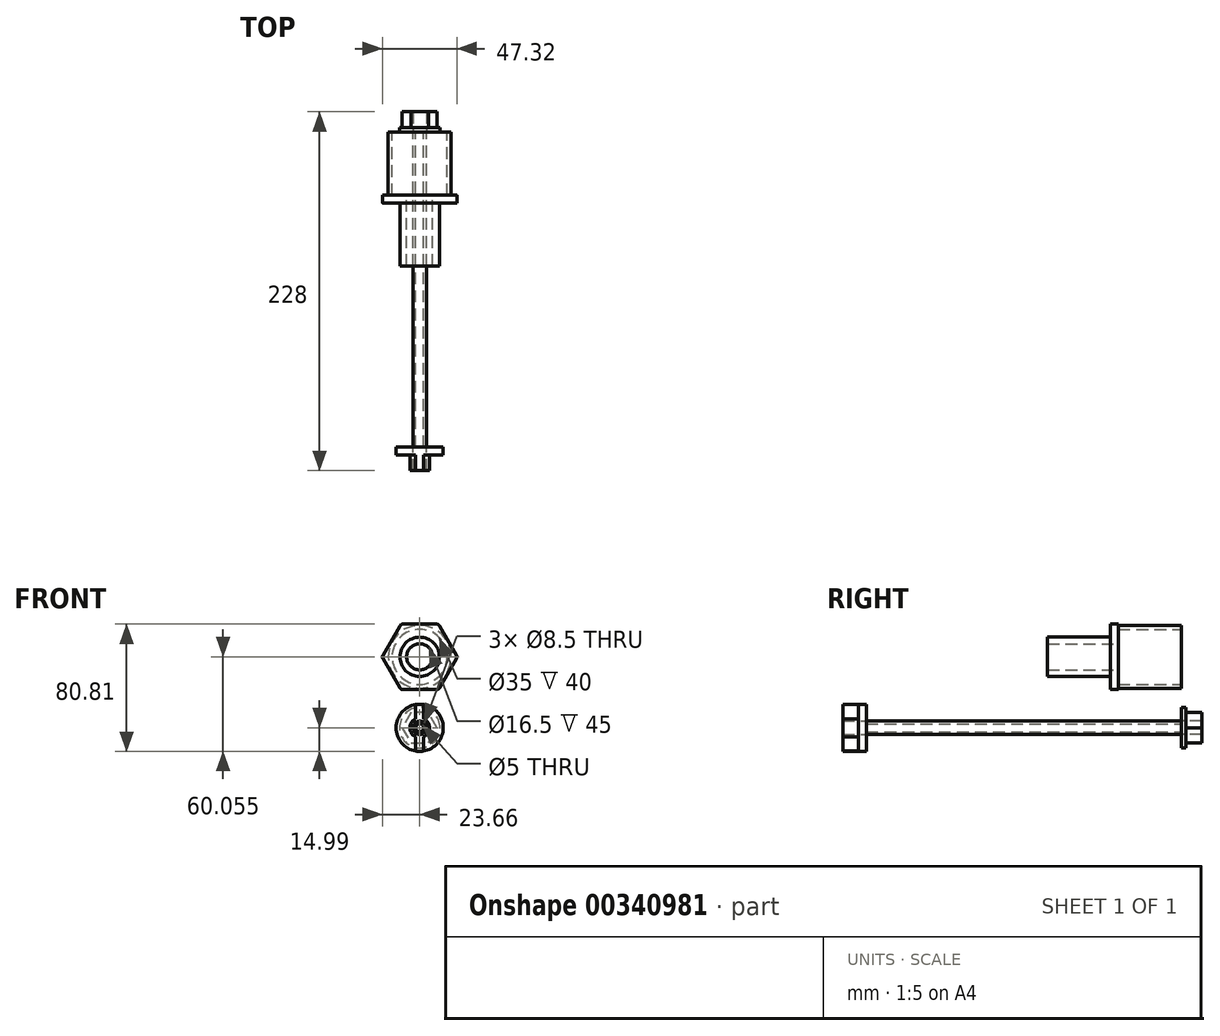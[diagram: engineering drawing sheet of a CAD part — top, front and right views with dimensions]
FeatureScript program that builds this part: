
annotation { "Feature Type Name" : "Feature", "Feature Type Description" : "" }
export const myFeature = defineFeature(function(context is Context, id is Id, definition is map)
    precondition{}
    {
        {
            var Q0;
            Q0=qCreatedBy(makeId("Front.planeOp"),FACE);
            var sketch = newSketch(context, id + "F0", { "sketchPlane" : qUnion([Q0])});
            skCircle(sketch, "E0", {"center": v(0, 0) * mm, "radius": 4.25 * mm});
            skCircle(sketch, "E1", {"center": v(0, 0) * mm, "radius": 2.5 * mm});
            skSolve(sketch);
        }
        {
            var Q0;
            Q0=makeQuery(id+"F0.imprint","IMPRINT",FACE,{"disambiguationData":[TD([[makeQuery(id+"F0.imprint","IMPRINT",EDGE,{"derivedFrom":sQuery(id+"F0.wireOp",EDGE,"E0")}),1.0]])]});
            extrude(context, id + "F1", {"entities" : qUnion([Q0]), "depth" : 200 * mm});
        }
        {
            var Q0;
            Q0=makeQuery(id+"F1.opExtrude","CAP_FACE",FACE,{"disambiguationData":[OSD([sQuery(id+"F0.wireOp",EDGE,"E0"),sQuery(id+"F0.wireOp",EDGE,"E1")])],"isStart":false});
            var sketch = newSketch(context, id + "F2", { "sketchPlane" : qUnion([Q0])});
            skCircle(sketch, "E2", {"center": v(0, 0) * mm, "radius": 4.25 * mm});
            skCircle(sketch, "E3", {"center": v(0, 0) * mm, "radius": 14.99 * mm});
            skSolve(sketch);
        }
        {
            var Q0;
            Q0=makeQuery(id+"F2.imprint","IMPRINT",FACE,{"disambiguationData":[TD([[makeQuery(id+"F2.imprint","IMPRINT",EDGE,{"derivedFrom":sQuery(id+"F2.wireOp",EDGE,"E2")}),-1.0]])]});
            extrude(context, id + "F3", {"entities" : qUnion([Q0]), "depth" : 5 * mm});
        }
        {
            var Q0;
            Q0=makeQuery(id+"F3.opExtrude","CAP_FACE",FACE,{"disambiguationData":[OSD([sQuery(id+"F2.wireOp",EDGE,"E2"),sQuery(id+"F2.wireOp",EDGE,"E3")])],"isStart":false});
            var sketch = newSketch(context, id + "F4", { "sketchPlane" : qUnion([Q0])});
            skCircle(sketch, "E4", {"center": v(0, 0) * mm, "radius": 14.99 * mm});
            skCircle(sketch, "E5", {"center": v(0, 0) * mm, "radius": 4.25 * mm});
            skCircle(sketch, "E6", {"center": v(0, 0) * mm, "radius": 6.25 * mm});
            skLineSegment(sketch, "E7", {"start": v(-2.5, 5.73) * mm, "end": v(-2.5, 14.78) * mm});
            skLineSegment(sketch, "E8", {"start": v(2.5, 5.73) * mm, "end": v(2.5, 14.78) * mm});
            skLineSegment(sketch, "E9", {"start": v(2.5, -5.73) * mm, "end": v(2.5, -14.78) * mm});
            skLineSegment(sketch, "E10", {"start": v(-2.5, -5.73) * mm, "end": v(-2.5, -14.78) * mm});
            skLineSegment(sketch, "E11", {"start": v(-2.5, 10.25) * mm, "end": v(0, 10.25) * mm, "construction": true});
            skLineSegment(sketch, "E12", {"start": v(0, 10.25) * mm, "end": v(2.5, 10.25) * mm, "construction": true});
            skLineSegment(sketch, "E13", {"start": v(-2.5, -10.25) * mm, "end": v(0, -10.25) * mm, "construction": true});
            skLineSegment(sketch, "E14", {"start": v(0, -10.25) * mm, "end": v(2.5, -10.25) * mm, "construction": true});
            skLineSegment(sketch, "E15", {"start": v(-2.5, -5.73) * mm, "end": v(-2.5, 5.73) * mm, "construction": true});
            skSolve(sketch);
        }
        {
            var Q0;
            {var subQ0=sQuery(id+"F4.wireOp",EDGE,"E7");Q0=makeQuery(id+"F4.imprint","IMPRINT",FACE,{"disambiguationData":[TD([[makeQuery(id+"F4.imprint","IMPRINT",EDGE,{"derivedFrom":subQ0}),-1.0]])]});}
            var Q1;
            {var subQ0=sQuery(id+"F4.wireOp",EDGE,"E9");Q1=makeQuery(id+"F4.imprint","IMPRINT",FACE,{"disambiguationData":[TD([[makeQuery(id+"F4.imprint","IMPRINT",EDGE,{"derivedFrom":subQ0}),-1.0]])]});}
            var Q2;
            Q2=makeQuery(id+"F4.imprint","IMPRINT",FACE,{"disambiguationData":[TD([[makeQuery(id+"F4.imprint","IMPRINT",EDGE,{"derivedFrom":sQuery(id+"F4.wireOp",EDGE,"E5")}),-1.0]])]});
            extrude(context, id + "F5", {"entities" : qUnion([Q0, Q1, Q2]), "operationType" : NewBodyOperationType.ADD, "depth" : 10 * mm});
        }
        {
            var Q0;
            Q0=qCreatedBy(makeId("Front.planeOp"),FACE);
            var sketch = newSketch(context, id + "F6", { "sketchPlane" : qUnion([Q0])});
            skCircle(sketch, "E16", {"center": v(0, 45.07) * mm, "radius": 17.5 * mm});
            skCircle(sketch, "E17", {"center": v(0, 45.07) * mm, "radius": 20 * mm});
            skSolve(sketch);
        }
        {
            var Q0;
            Q0=qSketchRegion(id+"F6",true);
            extrude(context, id + "F7", {"entities" : qUnion([Q0]), "depth" : 40 * mm});
        }
        {
            var Q0;
            Q0=makeQuery(id+"F7.opExtrude","CAP_FACE",FACE,{"disambiguationData":[OSD([sQuery(id+"F6.wireOp",EDGE,"E16"),sQuery(id+"F6.wireOp",EDGE,"E17")])],"isStart":false});
            var sketch = newSketch(context, id + "F8", { "sketchPlane" : qUnion([Q0])});
            skCircle(sketch, "E18.cCircle", {"center": v(0, 45.07) * mm, "radius": 20.76 * mm, "construction": true});
            skLineSegment(sketch, "E18.0", {"start": v(-10.83, 65.82) * mm, "end": v(10.83, 65.82) * mm});
            skLineSegment(sketch, "E18.1", {"start": v(12.56, 64.82) * mm, "end": v(23.4, 46.07) * mm});
            skLineSegment(sketch, "E18.2", {"start": v(23.4, 44.07) * mm, "end": v(12.56, 25.3) * mm});
            skLineSegment(sketch, "E18.3", {"start": v(10.83, 24.3) * mm, "end": v(-10.83, 24.3) * mm});
            skLineSegment(sketch, "E18.4", {"start": v(-12.56, 25.3) * mm, "end": v(-23.4, 44.07) * mm});
            skLineSegment(sketch, "E18.5", {"start": v(-23.4, 46.07) * mm, "end": v(-12.56, 64.82) * mm});
            skPoint(sketch, "E18.0.midPoint", {"position": v(0, 65.82) * mm});
            skCircle(sketch, "E19", {"center": v(0, 45.07) * mm, "radius": 8.25 * mm});
            skPoint(sketch, "E20.visualSharp", {"position": v(-23.97, 45.07) * mm});
            skArc(sketch, "E20.filletArc", {"start": v(-23.4, 46.07) * mm, "mid": v(-23.66, 45.07) * mm, "end": v(-23.4, 44.07) * mm});
            skPoint(sketch, "E21.visualSharp", {"position": v(-11.98, 24.3) * mm});
            skArc(sketch, "E21.filletArc", {"start": v(-12.56, 25.3) * mm, "mid": v(-11.83, 24.58) * mm, "end": v(-10.83, 24.3) * mm});
            skPoint(sketch, "E22.visualSharp", {"position": v(11.98, 24.3) * mm});
            skArc(sketch, "E22.filletArc", {"start": v(10.83, 24.3) * mm, "mid": v(11.83, 24.58) * mm, "end": v(12.56, 25.3) * mm});
            skPoint(sketch, "E23.visualSharp", {"position": v(23.97, 45.07) * mm});
            skArc(sketch, "E23.filletArc", {"start": v(23.4, 44.07) * mm, "mid": v(23.66, 45.07) * mm, "end": v(23.4, 46.07) * mm});
            skPoint(sketch, "E24.visualSharp", {"position": v(11.98, 65.82) * mm});
            skArc(sketch, "E24.filletArc", {"start": v(12.56, 64.82) * mm, "mid": v(11.83, 65.55) * mm, "end": v(10.83, 65.82) * mm});
            skPoint(sketch, "E25.visualSharp", {"position": v(-11.98, 65.82) * mm});
            skArc(sketch, "E25.filletArc", {"start": v(-10.83, 65.82) * mm, "mid": v(-11.83, 65.55) * mm, "end": v(-12.56, 64.82) * mm});
            skSolve(sketch);
        }
        {
            var Q0;
            Q0=qSketchRegion(id+"F8",true);
            extrude(context, id + "F9", {"entities" : qUnion([Q0]), "operationType" : NewBodyOperationType.ADD, "depth" : 5 * mm});
        }
        {
            var Q0;
            Q0=makeQuery(id+"F9.opExtrude","CAP_FACE",FACE,{"disambiguationData":[OSD([sQuery(id+"F8.wireOp",EDGE,"E18.0"),sQuery(id+"F8.wireOp",EDGE,"E18.1"),sQuery(id+"F8.wireOp",EDGE,"E18.2"),sQuery(id+"F8.wireOp",EDGE,"E18.3"),sQuery(id+"F8.wireOp",EDGE,"E18.4"),sQuery(id+"F8.wireOp",EDGE,"E18.5"),sQuery(id+"F8.wireOp",EDGE,"E19"),sQuery(id+"F8.wireOp",EDGE,"E20.filletArc"),sQuery(id+"F8.wireOp",EDGE,"E21.filletArc"),sQuery(id+"F8.wireOp",EDGE,"E22.filletArc"),sQuery(id+"F8.wireOp",EDGE,"E23.filletArc"),sQuery(id+"F8.wireOp",EDGE,"E24.filletArc"),sQuery(id+"F8.wireOp",EDGE,"E25.filletArc")])],"isStart":false});
            var sketch = newSketch(context, id + "F10", { "sketchPlane" : qUnion([Q0])});
            skCircle(sketch, "E26", {"center": v(0, 45.07) * mm, "radius": 8.25 * mm});
            skCircle(sketch, "E27", {"center": v(0, 45.07) * mm, "radius": 12.5 * mm});
            skSolve(sketch);
        }
        {
            var Q0;
            Q0=qSketchRegion(id+"F10",true);
            extrude(context, id + "F11", {"entities" : qUnion([Q0]), "operationType" : NewBodyOperationType.ADD, "depth" : 40 * mm});
        }
        {
            var Q0;
            Q0=makeQuery(id+"F1.opExtrude","CAP_FACE",FACE,{"disambiguationData":[OSD([sQuery(id+"F0.wireOp",EDGE,"E0"),sQuery(id+"F0.wireOp",EDGE,"E1")])],"isStart":true});
            var sketch = newSketch(context, id + "F12", { "sketchPlane" : qUnion([Q0])});
            skCircle(sketch, "E28", {"center": v(0, 0) * mm, "radius": 4.25 * mm});
            skCircle(sketch, "E29", {"center": v(0, 0) * mm, "radius": 12.87 * mm});
            skSolve(sketch);
        }
        {
            var Q0;
            Q0=qSketchRegion(id+"F12",true);
            extrude(context, id + "F13", {"entities" : qUnion([Q0]), "depth" : 3 * mm});
        }
        {
            var Q0;
            Q0=makeQuery(id+"F13.opExtrude","CAP_FACE",FACE,{"disambiguationData":[OSD([sQuery(id+"F12.wireOp",EDGE,"E28"),sQuery(id+"F12.wireOp",EDGE,"E29")])],"isStart":false});
            var sketch = newSketch(context, id + "F14", { "sketchPlane" : qUnion([Q0])});
            skCircle(sketch, "E30.cCircle", {"center": v(0, 0) * mm, "radius": 9.63 * mm, "construction": true});
            skLineSegment(sketch, "E30.0", {"start": v(-5.56, 9.63) * mm, "end": v(5.56, 9.63) * mm});
            skLineSegment(sketch, "E30.1", {"start": v(5.56, 9.63) * mm, "end": v(11.12, 0) * mm});
            skLineSegment(sketch, "E30.2", {"start": v(11.12, 0) * mm, "end": v(5.56, -9.63) * mm});
            skLineSegment(sketch, "E30.3", {"start": v(5.56, -9.63) * mm, "end": v(-5.56, -9.63) * mm});
            skLineSegment(sketch, "E30.4", {"start": v(-5.56, -9.63) * mm, "end": v(-11.12, 0) * mm});
            skLineSegment(sketch, "E30.5", {"start": v(-11.12, 0) * mm, "end": v(-5.56, 9.63) * mm});
            skPoint(sketch, "E30.0.midPoint", {"position": v(0, 9.63) * mm});
            skCircle(sketch, "E31", {"center": v(0, 0) * mm, "radius": 4.25 * mm});
            skSolve(sketch);
        }
        {
            var Q0;
            Q0 = qSketchRegion(id + "F14", true);
            extrude(context, id + "F15", {"entities" : qUnion([Q0]), "depth" : 10 * mm});
        }
    });
